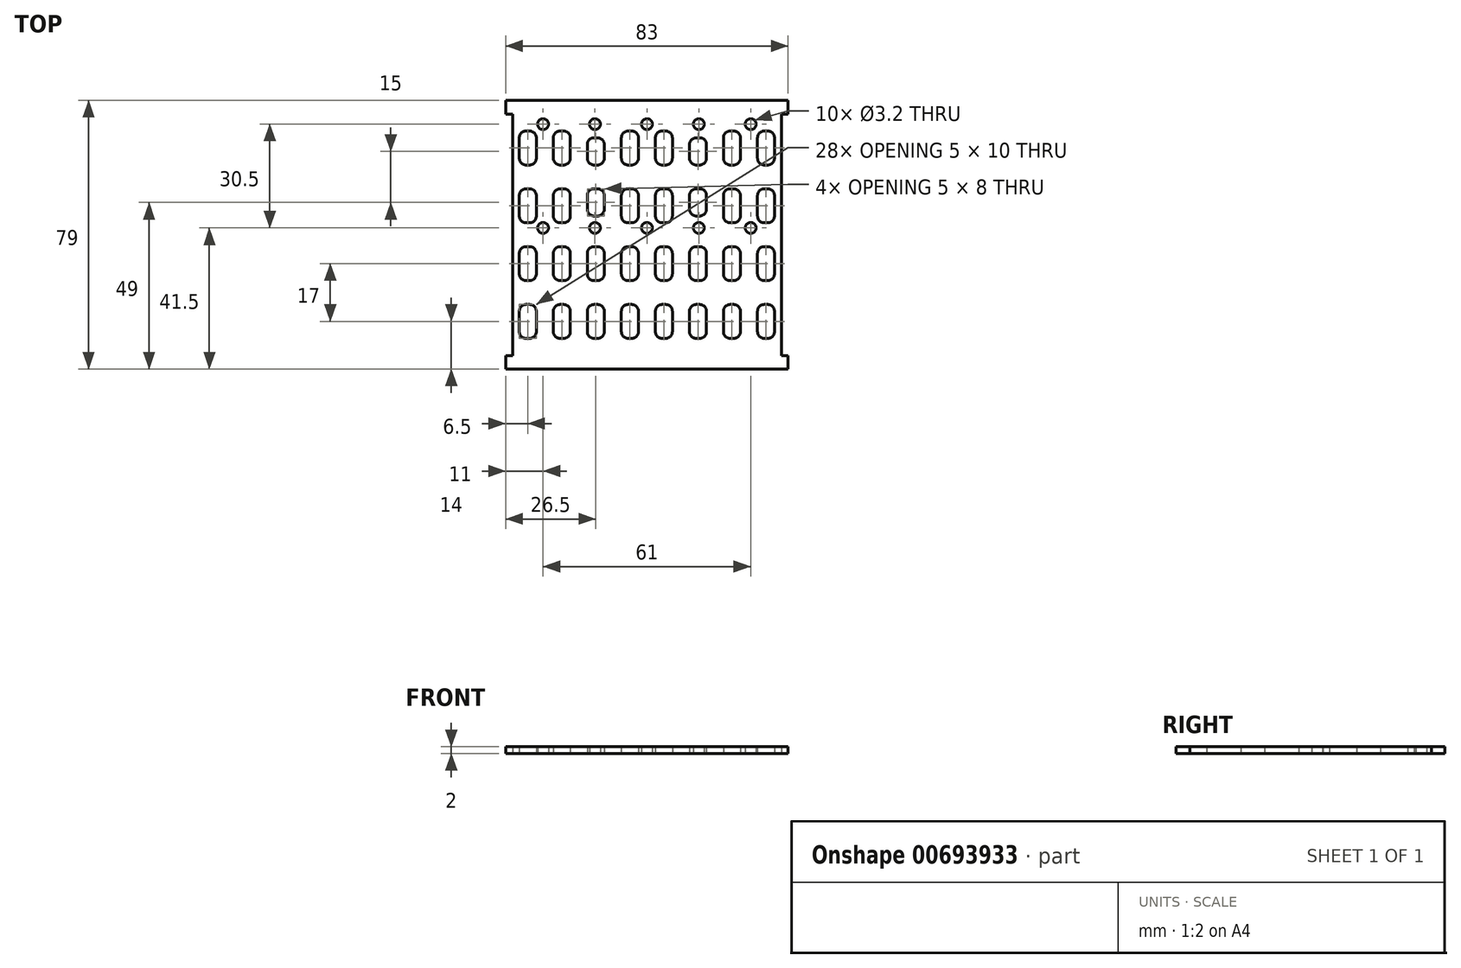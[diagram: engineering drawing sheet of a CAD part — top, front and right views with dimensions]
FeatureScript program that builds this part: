
annotation { "Feature Type Name" : "Feature", "Feature Type Description" : "" }
export const myFeature = defineFeature(function(context is Context, id is Id, definition is map)
    precondition{}
    {
        {
            var Q0;
            Q0=qCreatedBy(makeId("Top.planeOp"),FACE);
            var sketch = newSketch(context, id + "F0", { "sketchPlane" : qUnion([Q0])});
            skLineSegment(sketch, "E0.bottom", {"start": v(39.5, 39.5) * mm, "end": v(-39.5, 39.5) * mm});
            skLineSegment(sketch, "E0.top", {"start": v(39.5, -39.5) * mm, "end": v(-39.5, -39.5) * mm});
            skLineSegment(sketch, "E0.left", {"start": v(39.5, 35.5) * mm, "end": v(39.5, -35.5) * mm});
            skLineSegment(sketch, "E0.right", {"start": v(-39.5, 35.5) * mm, "end": v(-39.5, -35.5) * mm});
            skPoint(sketch, "E0.middle", {"position": v(0, 0) * mm});
            skCircle(sketch, "E1", {"center": v(-30.5, 32.5) * mm, "radius": 1.6 * mm});
            skCircle(sketch, "E2.0.1.0", {"center": v(-30.5, 2) * mm, "radius": 1.6 * mm});
            skCircle(sketch, "E2.1.0.0", {"center": v(-15.25, 32.5) * mm, "radius": 1.6 * mm});
            skCircle(sketch, "E2.1.1.0", {"center": v(-15.25, 2) * mm, "radius": 1.6 * mm});
            skLineSegment(sketch, "E2.direction1", {"start": v(-30.5, 32.5) * mm, "end": v(-15.25, 32.5) * mm, "construction": true});
            skLineSegment(sketch, "E2.direction2", {"start": v(-30.5, 32.5) * mm, "end": v(-30.5, 2) * mm, "construction": true});
            skCircle(sketch, "E3.0.2.0", {"center": v(0, 32.5) * mm, "radius": 1.6 * mm});
            skCircle(sketch, "E3.0.2.1", {"center": v(0, 2) * mm, "radius": 1.6 * mm});
            skCircle(sketch, "E3.0.3.0", {"center": v(15.25, 32.5) * mm, "radius": 1.6 * mm});
            skCircle(sketch, "E3.0.3.1", {"center": v(15.25, 2) * mm, "radius": 1.6 * mm});
            skCircle(sketch, "E3.0.4.0", {"center": v(30.5, 32.5) * mm, "radius": 1.6 * mm});
            skCircle(sketch, "E3.0.4.1", {"center": v(30.5, 2) * mm, "radius": 1.6 * mm});
            skLineSegment(sketch, "E4.bottom", {"start": v(-5.5, -3.5) * mm, "end": v(-4.5, -3.5) * mm});
            skLineSegment(sketch, "E4.top", {"start": v(-5.5, -13.5) * mm, "end": v(-4.5, -13.5) * mm});
            skLineSegment(sketch, "E4.left", {"start": v(-7.5, -5.5) * mm, "end": v(-7.5, -11.5) * mm});
            skLineSegment(sketch, "E4.right", {"start": v(-2.5, -5.5) * mm, "end": v(-2.5, -11.5) * mm});
            skPoint(sketch, "E5.visualSharp", {"position": v(-7.5, -3.5) * mm});
            skArc(sketch, "E5.filletArc", {"start": v(-5.5, -3.5) * mm, "mid": v(-6.91, -4.09) * mm, "end": v(-7.5, -5.5) * mm});
            skPoint(sketch, "E6.visualSharp", {"position": v(-2.5, -3.5) * mm});
            skArc(sketch, "E6.filletArc", {"start": v(-2.5, -5.5) * mm, "mid": v(-3.09, -4.09) * mm, "end": v(-4.5, -3.5) * mm});
            skPoint(sketch, "E7.visualSharp", {"position": v(-7.5, -13.5) * mm});
            skArc(sketch, "E7.filletArc", {"start": v(-7.5, -11.5) * mm, "mid": v(-6.91, -12.91) * mm, "end": v(-5.5, -13.5) * mm});
            skPoint(sketch, "E8.visualSharp", {"position": v(-2.5, -13.5) * mm});
            skArc(sketch, "E8.filletArc", {"start": v(-4.5, -13.5) * mm, "mid": v(-3.09, -12.91) * mm, "end": v(-2.5, -11.5) * mm});
            skLineSegment(sketch, "E9.0.1.0", {"start": v(-7.5, -22.5) * mm, "end": v(-7.5, -28.5) * mm});
            skLineSegment(sketch, "E9.0.1.1", {"start": v(-2.5, -22.5) * mm, "end": v(-2.5, -28.5) * mm});
            skArc(sketch, "E9.0.1.2", {"start": v(-2.5, -22.5) * mm, "mid": v(-3.09, -21.09) * mm, "end": v(-4.5, -20.5) * mm});
            skLineSegment(sketch, "E9.0.1.3", {"start": v(-5.5, -20.5) * mm, "end": v(-4.5, -20.5) * mm});
            skArc(sketch, "E9.0.1.4", {"start": v(-5.5, -20.5) * mm, "mid": v(-6.91, -21.09) * mm, "end": v(-7.5, -22.5) * mm});
            skArc(sketch, "E9.0.1.5", {"start": v(-7.5, -28.5) * mm, "mid": v(-6.91, -29.91) * mm, "end": v(-5.5, -30.5) * mm});
            skLineSegment(sketch, "E9.0.1.6", {"start": v(-5.5, -30.5) * mm, "end": v(-4.5, -30.5) * mm});
            skArc(sketch, "E9.0.1.7", {"start": v(-4.5, -30.5) * mm, "mid": v(-3.09, -29.91) * mm, "end": v(-2.5, -28.5) * mm});
            skLineSegment(sketch, "E9.1.0.0", {"start": v(-17.5, -5.5) * mm, "end": v(-17.5, -11.5) * mm});
            skLineSegment(sketch, "E9.1.0.1", {"start": v(-12.5, -5.5) * mm, "end": v(-12.5, -11.5) * mm});
            skArc(sketch, "E9.1.0.2", {"start": v(-12.5, -5.5) * mm, "mid": v(-13.09, -4.09) * mm, "end": v(-14.5, -3.5) * mm});
            skLineSegment(sketch, "E9.1.0.3", {"start": v(-15.5, -3.5) * mm, "end": v(-14.5, -3.5) * mm});
            skArc(sketch, "E9.1.0.4", {"start": v(-15.5, -3.5) * mm, "mid": v(-16.91, -4.09) * mm, "end": v(-17.5, -5.5) * mm});
            skArc(sketch, "E9.1.0.5", {"start": v(-17.5, -11.5) * mm, "mid": v(-16.91, -12.91) * mm, "end": v(-15.5, -13.5) * mm});
            skLineSegment(sketch, "E9.1.0.6", {"start": v(-15.5, -13.5) * mm, "end": v(-14.5, -13.5) * mm});
            skArc(sketch, "E9.1.0.7", {"start": v(-14.5, -13.5) * mm, "mid": v(-13.09, -12.91) * mm, "end": v(-12.5, -11.5) * mm});
            skLineSegment(sketch, "E9.1.1.0", {"start": v(-17.5, -22.5) * mm, "end": v(-17.5, -28.5) * mm});
            skLineSegment(sketch, "E9.1.1.1", {"start": v(-12.5, -22.5) * mm, "end": v(-12.5, -28.5) * mm});
            skArc(sketch, "E9.1.1.2", {"start": v(-12.5, -22.5) * mm, "mid": v(-13.09, -21.09) * mm, "end": v(-14.5, -20.5) * mm});
            skLineSegment(sketch, "E9.1.1.3", {"start": v(-15.5, -20.5) * mm, "end": v(-14.5, -20.5) * mm});
            skArc(sketch, "E9.1.1.4", {"start": v(-15.5, -20.5) * mm, "mid": v(-16.91, -21.09) * mm, "end": v(-17.5, -22.5) * mm});
            skArc(sketch, "E9.1.1.5", {"start": v(-17.5, -28.5) * mm, "mid": v(-16.91, -29.91) * mm, "end": v(-15.5, -30.5) * mm});
            skLineSegment(sketch, "E9.1.1.6", {"start": v(-15.5, -30.5) * mm, "end": v(-14.5, -30.5) * mm});
            skArc(sketch, "E9.1.1.7", {"start": v(-14.5, -30.5) * mm, "mid": v(-13.09, -29.91) * mm, "end": v(-12.5, -28.5) * mm});
            skLineSegment(sketch, "E9.2.0.0", {"start": v(-27.5, -5.5) * mm, "end": v(-27.5, -11.5) * mm});
            skLineSegment(sketch, "E9.2.0.1", {"start": v(-22.5, -5.5) * mm, "end": v(-22.5, -11.5) * mm});
            skArc(sketch, "E9.2.0.2", {"start": v(-22.5, -5.5) * mm, "mid": v(-23.09, -4.09) * mm, "end": v(-24.5, -3.5) * mm});
            skLineSegment(sketch, "E9.2.0.3", {"start": v(-25.5, -3.5) * mm, "end": v(-24.5, -3.5) * mm});
            skArc(sketch, "E9.2.0.4", {"start": v(-25.5, -3.5) * mm, "mid": v(-26.91, -4.09) * mm, "end": v(-27.5, -5.5) * mm});
            skArc(sketch, "E9.2.0.5", {"start": v(-27.5, -11.5) * mm, "mid": v(-26.91, -12.91) * mm, "end": v(-25.5, -13.5) * mm});
            skLineSegment(sketch, "E9.2.0.6", {"start": v(-25.5, -13.5) * mm, "end": v(-24.5, -13.5) * mm});
            skArc(sketch, "E9.2.0.7", {"start": v(-24.5, -13.5) * mm, "mid": v(-23.09, -12.91) * mm, "end": v(-22.5, -11.5) * mm});
            skLineSegment(sketch, "E9.2.1.0", {"start": v(-27.5, -22.5) * mm, "end": v(-27.5, -28.5) * mm});
            skLineSegment(sketch, "E9.2.1.1", {"start": v(-22.5, -22.5) * mm, "end": v(-22.5, -28.5) * mm});
            skArc(sketch, "E9.2.1.2", {"start": v(-22.5, -22.5) * mm, "mid": v(-23.09, -21.09) * mm, "end": v(-24.5, -20.5) * mm});
            skLineSegment(sketch, "E9.2.1.3", {"start": v(-25.5, -20.5) * mm, "end": v(-24.5, -20.5) * mm});
            skArc(sketch, "E9.2.1.4", {"start": v(-25.5, -20.5) * mm, "mid": v(-26.91, -21.09) * mm, "end": v(-27.5, -22.5) * mm});
            skArc(sketch, "E9.2.1.5", {"start": v(-27.5, -28.5) * mm, "mid": v(-26.91, -29.91) * mm, "end": v(-25.5, -30.5) * mm});
            skLineSegment(sketch, "E9.2.1.6", {"start": v(-25.5, -30.5) * mm, "end": v(-24.5, -30.5) * mm});
            skArc(sketch, "E9.2.1.7", {"start": v(-24.5, -30.5) * mm, "mid": v(-23.09, -29.91) * mm, "end": v(-22.5, -28.5) * mm});
            skLineSegment(sketch, "E9.3.0.0", {"start": v(-37.5, -5.5) * mm, "end": v(-37.5, -11.5) * mm});
            skLineSegment(sketch, "E9.3.0.1", {"start": v(-32.5, -5.5) * mm, "end": v(-32.5, -11.5) * mm});
            skArc(sketch, "E9.3.0.2", {"start": v(-32.5, -5.5) * mm, "mid": v(-33.09, -4.09) * mm, "end": v(-34.5, -3.5) * mm});
            skLineSegment(sketch, "E9.3.0.3", {"start": v(-35.5, -3.5) * mm, "end": v(-34.5, -3.5) * mm});
            skArc(sketch, "E9.3.0.4", {"start": v(-35.5, -3.5) * mm, "mid": v(-36.91, -4.09) * mm, "end": v(-37.5, -5.5) * mm});
            skArc(sketch, "E9.3.0.5", {"start": v(-37.5, -11.5) * mm, "mid": v(-36.91, -12.91) * mm, "end": v(-35.5, -13.5) * mm});
            skLineSegment(sketch, "E9.3.0.6", {"start": v(-35.5, -13.5) * mm, "end": v(-34.5, -13.5) * mm});
            skArc(sketch, "E9.3.0.7", {"start": v(-34.5, -13.5) * mm, "mid": v(-33.09, -12.91) * mm, "end": v(-32.5, -11.5) * mm});
            skLineSegment(sketch, "E9.3.1.0", {"start": v(-37.5, -22.5) * mm, "end": v(-37.5, -28.5) * mm});
            skLineSegment(sketch, "E9.3.1.1", {"start": v(-32.5, -22.5) * mm, "end": v(-32.5, -28.5) * mm});
            skArc(sketch, "E9.3.1.2", {"start": v(-32.5, -22.5) * mm, "mid": v(-33.09, -21.09) * mm, "end": v(-34.5, -20.5) * mm});
            skLineSegment(sketch, "E9.3.1.3", {"start": v(-35.5, -20.5) * mm, "end": v(-34.5, -20.5) * mm});
            skArc(sketch, "E9.3.1.4", {"start": v(-35.5, -20.5) * mm, "mid": v(-36.91, -21.09) * mm, "end": v(-37.5, -22.5) * mm});
            skArc(sketch, "E9.3.1.5", {"start": v(-37.5, -28.5) * mm, "mid": v(-36.91, -29.91) * mm, "end": v(-35.5, -30.5) * mm});
            skLineSegment(sketch, "E9.3.1.6", {"start": v(-35.5, -30.5) * mm, "end": v(-34.5, -30.5) * mm});
            skArc(sketch, "E9.3.1.7", {"start": v(-34.5, -30.5) * mm, "mid": v(-33.09, -29.91) * mm, "end": v(-32.5, -28.5) * mm});
            skLineSegment(sketch, "E9.direction1", {"start": v(-7.5, -11.5) * mm, "end": v(-17.5, -11.5) * mm, "construction": true});
            skLineSegment(sketch, "E9.direction2", {"start": v(-7.5, -11.5) * mm, "end": v(-7.5, -28.5) * mm, "construction": true});
            skLineSegment(sketch, "E10.0.1.0", {"start": v(-37.5, 28.5) * mm, "end": v(-37.5, 22.5) * mm});
            skLineSegment(sketch, "E10.0.1.1", {"start": v(-22.5, 11.5) * mm, "end": v(-22.5, 5.5) * mm});
            skLineSegment(sketch, "E10.0.1.2", {"start": v(-12.5, 11.5) * mm, "end": v(-12.5, 7.5) * mm});
            skLineSegment(sketch, "E10.0.1.3", {"start": v(-2.5, 28.5) * mm, "end": v(-2.5, 22.5) * mm});
            skLineSegment(sketch, "E10.0.1.4", {"start": v(-2.5, 11.5) * mm, "end": v(-2.5, 5.5) * mm});
            skLineSegment(sketch, "E10.0.1.5", {"start": v(-12.5, 26.5) * mm, "end": v(-12.5, 22.5) * mm});
            skLineSegment(sketch, "E10.0.1.6", {"start": v(-27.5, 11.5) * mm, "end": v(-27.5, 5.5) * mm});
            skLineSegment(sketch, "E10.0.1.7", {"start": v(-27.5, 28.5) * mm, "end": v(-27.5, 22.5) * mm});
            skLineSegment(sketch, "E10.0.1.8", {"start": v(-32.5, 11.5) * mm, "end": v(-32.5, 5.5) * mm});
            skLineSegment(sketch, "E10.0.1.9", {"start": v(-7.5, 28.5) * mm, "end": v(-7.5, 22.5) * mm});
            skLineSegment(sketch, "E10.0.1.10", {"start": v(-17.5, 11.5) * mm, "end": v(-17.5, 7.5) * mm});
            skLineSegment(sketch, "E10.0.1.11", {"start": v(-22.5, 28.5) * mm, "end": v(-22.5, 22.5) * mm});
            skLineSegment(sketch, "E10.0.1.12", {"start": v(-7.5, 22.5) * mm, "end": v(-17.5, 22.5) * mm, "construction": true});
            skLineSegment(sketch, "E10.0.1.13", {"start": v(-37.5, 11.5) * mm, "end": v(-37.5, 5.5) * mm});
            skLineSegment(sketch, "E10.0.1.14", {"start": v(-32.5, 28.5) * mm, "end": v(-32.5, 22.5) * mm});
            skLineSegment(sketch, "E10.0.1.15", {"start": v(-17.5, 26.5) * mm, "end": v(-17.5, 22.5) * mm});
            skLineSegment(sketch, "E10.0.1.16", {"start": v(-7.5, 11.5) * mm, "end": v(-7.5, 5.5) * mm});
            skArc(sketch, "E10.0.1.17", {"start": v(-32.5, 11.5) * mm, "mid": v(-33.09, 12.91) * mm, "end": v(-34.5, 13.5) * mm});
            skArc(sketch, "E10.0.1.18", {"start": v(-2.5, 28.5) * mm, "mid": v(-3.09, 29.91) * mm, "end": v(-4.5, 30.5) * mm});
            skLineSegment(sketch, "E10.0.1.19", {"start": v(-25.5, 13.5) * mm, "end": v(-24.5, 13.5) * mm});
            skArc(sketch, "E10.0.1.20", {"start": v(-2.5, 11.5) * mm, "mid": v(-3.09, 12.91) * mm, "end": v(-4.5, 13.5) * mm});
            skArc(sketch, "E10.0.1.21", {"start": v(-37.5, 5.5) * mm, "mid": v(-36.91, 4.09) * mm, "end": v(-35.5, 3.5) * mm});
            skArc(sketch, "E10.0.1.22", {"start": v(-32.5, 28.5) * mm, "mid": v(-33.09, 29.91) * mm, "end": v(-34.5, 30.5) * mm});
            skArc(sketch, "E10.0.1.23", {"start": v(-35.5, 13.5) * mm, "mid": v(-36.91, 12.91) * mm, "end": v(-37.5, 11.5) * mm});
            skLineSegment(sketch, "E10.0.1.24", {"start": v(-5.5, 13.5) * mm, "end": v(-4.5, 13.5) * mm});
            skArc(sketch, "E10.0.1.25", {"start": v(-22.5, 28.5) * mm, "mid": v(-23.09, 29.91) * mm, "end": v(-24.5, 30.5) * mm});
            skArc(sketch, "E10.0.1.26", {"start": v(-15.5, 13.5) * mm, "mid": v(-16.91, 12.91) * mm, "end": v(-17.5, 11.5) * mm});
            skLineSegment(sketch, "E10.0.1.27", {"start": v(-35.5, 30.5) * mm, "end": v(-34.5, 30.5) * mm});
            skArc(sketch, "E10.0.1.28", {"start": v(-12.5, 11.5) * mm, "mid": v(-13.09, 12.91) * mm, "end": v(-14.5, 13.5) * mm});
            skLineSegment(sketch, "E10.0.1.29", {"start": v(-35.5, 13.5) * mm, "end": v(-34.5, 13.5) * mm});
            skArc(sketch, "E10.0.1.32", {"start": v(-4.5, 3.5) * mm, "mid": v(-3.09, 4.09) * mm, "end": v(-2.5, 5.5) * mm});
            skArc(sketch, "E10.0.1.33", {"start": v(-5.5, 13.5) * mm, "mid": v(-6.91, 12.91) * mm, "end": v(-7.5, 11.5) * mm});
            skArc(sketch, "E10.0.1.34", {"start": v(-5.5, 30.5) * mm, "mid": v(-6.91, 29.91) * mm, "end": v(-7.5, 28.5) * mm});
            skArc(sketch, "E10.0.1.35", {"start": v(-35.5, 30.5) * mm, "mid": v(-36.91, 29.91) * mm, "end": v(-37.5, 28.5) * mm});
            skLineSegment(sketch, "E10.0.1.36", {"start": v(-35.5, 20.5) * mm, "end": v(-34.5, 20.5) * mm});
            skArc(sketch, "E10.0.1.38", {"start": v(-34.5, 3.5) * mm, "mid": v(-33.09, 4.09) * mm, "end": v(-32.5, 5.5) * mm});
            skArc(sketch, "E10.0.1.39", {"start": v(-37.5, 22.5) * mm, "mid": v(-36.91, 21.09) * mm, "end": v(-35.5, 20.5) * mm});
            skArc(sketch, "E10.0.1.40", {"start": v(-14.5, 20.5) * mm, "mid": v(-13.09, 21.09) * mm, "end": v(-12.5, 22.5) * mm});
            skLineSegment(sketch, "E10.0.1.42", {"start": v(-15.5, 13.5) * mm, "end": v(-14.5, 13.5) * mm});
            skArc(sketch, "E10.0.1.43", {"start": v(-22.5, 11.5) * mm, "mid": v(-23.09, 12.91) * mm, "end": v(-24.5, 13.5) * mm});
            skArc(sketch, "E10.0.1.44", {"start": v(-25.5, 30.5) * mm, "mid": v(-26.91, 29.91) * mm, "end": v(-27.5, 28.5) * mm});
            skArc(sketch, "E10.0.1.45", {"start": v(-27.5, 5.5) * mm, "mid": v(-26.91, 4.09) * mm, "end": v(-25.5, 3.5) * mm});
            skArc(sketch, "E10.0.1.46", {"start": v(-4.5, 20.5) * mm, "mid": v(-3.09, 21.09) * mm, "end": v(-2.5, 22.5) * mm});
            skLineSegment(sketch, "E10.0.1.47", {"start": v(-25.5, 20.5) * mm, "end": v(-24.5, 20.5) * mm});
            skLineSegment(sketch, "E10.0.1.48", {"start": v(-5.5, 3.5) * mm, "end": v(-4.5, 3.5) * mm});
            skArc(sketch, "E10.0.1.50", {"start": v(-24.5, 20.5) * mm, "mid": v(-23.09, 21.09) * mm, "end": v(-22.5, 22.5) * mm});
            skArc(sketch, "E10.0.1.51", {"start": v(-34.5, 20.5) * mm, "mid": v(-33.09, 21.09) * mm, "end": v(-32.5, 22.5) * mm});
            skArc(sketch, "E10.0.1.53", {"start": v(-17.5, 22.5) * mm, "mid": v(-16.91, 21.09) * mm, "end": v(-15.5, 20.5) * mm});
            skArc(sketch, "E10.0.1.54", {"start": v(-24.5, 3.5) * mm, "mid": v(-23.09, 4.09) * mm, "end": v(-22.5, 5.5) * mm});
            skLineSegment(sketch, "E10.0.1.55", {"start": v(-35.5, 3.5) * mm, "end": v(-34.5, 3.5) * mm});
            skLineSegment(sketch, "E10.0.1.56", {"start": v(-15.5, 20.5) * mm, "end": v(-14.5, 20.5) * mm});
            skLineSegment(sketch, "E10.0.1.57", {"start": v(-25.5, 30.5) * mm, "end": v(-24.5, 30.5) * mm});
            skArc(sketch, "E10.0.1.58", {"start": v(-7.5, 5.5) * mm, "mid": v(-6.91, 4.09) * mm, "end": v(-5.5, 3.5) * mm});
            skArc(sketch, "E10.0.1.59", {"start": v(-27.5, 22.5) * mm, "mid": v(-26.91, 21.09) * mm, "end": v(-25.5, 20.5) * mm});
            skArc(sketch, "E10.0.1.60", {"start": v(-25.5, 13.5) * mm, "mid": v(-26.91, 12.91) * mm, "end": v(-27.5, 11.5) * mm});
            skLineSegment(sketch, "E10.0.1.61", {"start": v(-25.5, 3.5) * mm, "end": v(-24.5, 3.5) * mm});
            skArc(sketch, "E10.0.1.62", {"start": v(-7.5, 22.5) * mm, "mid": v(-6.91, 21.09) * mm, "end": v(-5.5, 20.5) * mm});
            skLineSegment(sketch, "E10.0.1.63", {"start": v(-5.5, 20.5) * mm, "end": v(-4.5, 20.5) * mm});
            skLineSegment(sketch, "E10.0.1.64", {"start": v(-5.5, 30.5) * mm, "end": v(-4.5, 30.5) * mm});
            skLineSegment(sketch, "E10.1.0.0", {"start": v(2.5, -5.5) * mm, "end": v(2.5, -11.5) * mm});
            skLineSegment(sketch, "E10.1.0.1", {"start": v(17.5, -22.5) * mm, "end": v(17.5, -28.5) * mm});
            skLineSegment(sketch, "E10.1.0.2", {"start": v(27.5, -22.5) * mm, "end": v(27.5, -28.5) * mm});
            skLineSegment(sketch, "E10.1.0.3", {"start": v(37.5, -5.5) * mm, "end": v(37.5, -11.5) * mm});
            skLineSegment(sketch, "E10.1.0.4", {"start": v(37.5, -22.5) * mm, "end": v(37.5, -28.5) * mm});
            skLineSegment(sketch, "E10.1.0.5", {"start": v(27.5, -5.5) * mm, "end": v(27.5, -11.5) * mm});
            skLineSegment(sketch, "E10.1.0.6", {"start": v(12.5, -22.5) * mm, "end": v(12.5, -28.5) * mm});
            skLineSegment(sketch, "E10.1.0.7", {"start": v(12.5, -5.5) * mm, "end": v(12.5, -11.5) * mm});
            skLineSegment(sketch, "E10.1.0.8", {"start": v(7.5, -22.5) * mm, "end": v(7.5, -28.5) * mm});
            skLineSegment(sketch, "E10.1.0.9", {"start": v(32.5, -5.5) * mm, "end": v(32.5, -11.5) * mm});
            skLineSegment(sketch, "E10.1.0.10", {"start": v(22.5, -22.5) * mm, "end": v(22.5, -28.5) * mm});
            skLineSegment(sketch, "E10.1.0.11", {"start": v(17.5, -5.5) * mm, "end": v(17.5, -11.5) * mm});
            skLineSegment(sketch, "E10.1.0.12", {"start": v(32.5, -11.5) * mm, "end": v(22.5, -11.5) * mm, "construction": true});
            skLineSegment(sketch, "E10.1.0.13", {"start": v(2.5, -22.5) * mm, "end": v(2.5, -28.5) * mm});
            skLineSegment(sketch, "E10.1.0.14", {"start": v(7.5, -5.5) * mm, "end": v(7.5, -11.5) * mm});
            skLineSegment(sketch, "E10.1.0.15", {"start": v(22.5, -5.5) * mm, "end": v(22.5, -11.5) * mm});
            skLineSegment(sketch, "E10.1.0.16", {"start": v(32.5, -22.5) * mm, "end": v(32.5, -28.5) * mm});
            skArc(sketch, "E10.1.0.17", {"start": v(7.5, -22.5) * mm, "mid": v(6.91, -21.09) * mm, "end": v(5.5, -20.5) * mm});
            skArc(sketch, "E10.1.0.18", {"start": v(37.5, -5.5) * mm, "mid": v(36.91, -4.09) * mm, "end": v(35.5, -3.5) * mm});
            skLineSegment(sketch, "E10.1.0.19", {"start": v(14.5, -20.5) * mm, "end": v(15.5, -20.5) * mm});
            skArc(sketch, "E10.1.0.20", {"start": v(37.5, -22.5) * mm, "mid": v(36.91, -21.09) * mm, "end": v(35.5, -20.5) * mm});
            skArc(sketch, "E10.1.0.21", {"start": v(2.5, -28.5) * mm, "mid": v(3.09, -29.91) * mm, "end": v(4.5, -30.5) * mm});
            skArc(sketch, "E10.1.0.22", {"start": v(7.5, -5.5) * mm, "mid": v(6.91, -4.09) * mm, "end": v(5.5, -3.5) * mm});
            skArc(sketch, "E10.1.0.23", {"start": v(4.5, -20.5) * mm, "mid": v(3.09, -21.09) * mm, "end": v(2.5, -22.5) * mm});
            skLineSegment(sketch, "E10.1.0.24", {"start": v(34.5, -20.5) * mm, "end": v(35.5, -20.5) * mm});
            skArc(sketch, "E10.1.0.25", {"start": v(17.5, -5.5) * mm, "mid": v(16.91, -4.09) * mm, "end": v(15.5, -3.5) * mm});
            skArc(sketch, "E10.1.0.26", {"start": v(24.5, -20.5) * mm, "mid": v(23.09, -21.09) * mm, "end": v(22.5, -22.5) * mm});
            skLineSegment(sketch, "E10.1.0.27", {"start": v(4.5, -3.5) * mm, "end": v(5.5, -3.5) * mm});
            skArc(sketch, "E10.1.0.28", {"start": v(27.5, -22.5) * mm, "mid": v(26.91, -21.09) * mm, "end": v(25.5, -20.5) * mm});
            skLineSegment(sketch, "E10.1.0.29", {"start": v(4.5, -20.5) * mm, "end": v(5.5, -20.5) * mm});
            skArc(sketch, "E10.1.0.30", {"start": v(27.5, -5.5) * mm, "mid": v(26.91, -4.09) * mm, "end": v(25.5, -3.5) * mm});
            skLineSegment(sketch, "E10.1.0.31", {"start": v(24.5, -30.5) * mm, "end": v(25.5, -30.5) * mm});
            skArc(sketch, "E10.1.0.32", {"start": v(35.5, -30.5) * mm, "mid": v(36.91, -29.91) * mm, "end": v(37.5, -28.5) * mm});
            skArc(sketch, "E10.1.0.33", {"start": v(34.5, -20.5) * mm, "mid": v(33.09, -21.09) * mm, "end": v(32.5, -22.5) * mm});
            skArc(sketch, "E10.1.0.34", {"start": v(34.5, -3.5) * mm, "mid": v(33.09, -4.09) * mm, "end": v(32.5, -5.5) * mm});
            skArc(sketch, "E10.1.0.35", {"start": v(4.5, -3.5) * mm, "mid": v(3.09, -4.09) * mm, "end": v(2.5, -5.5) * mm});
            skLineSegment(sketch, "E10.1.0.36", {"start": v(4.5, -13.5) * mm, "end": v(5.5, -13.5) * mm});
            skArc(sketch, "E10.1.0.37", {"start": v(24.5, -3.5) * mm, "mid": v(23.09, -4.09) * mm, "end": v(22.5, -5.5) * mm});
            skArc(sketch, "E10.1.0.38", {"start": v(5.5, -30.5) * mm, "mid": v(6.91, -29.91) * mm, "end": v(7.5, -28.5) * mm});
            skArc(sketch, "E10.1.0.39", {"start": v(2.5, -11.5) * mm, "mid": v(3.09, -12.91) * mm, "end": v(4.5, -13.5) * mm});
            skArc(sketch, "E10.1.0.40", {"start": v(25.5, -13.5) * mm, "mid": v(26.91, -12.91) * mm, "end": v(27.5, -11.5) * mm});
            skLineSegment(sketch, "E10.1.0.41", {"start": v(24.5, -3.5) * mm, "end": v(25.5, -3.5) * mm});
            skLineSegment(sketch, "E10.1.0.42", {"start": v(24.5, -20.5) * mm, "end": v(25.5, -20.5) * mm});
            skArc(sketch, "E10.1.0.43", {"start": v(17.5, -22.5) * mm, "mid": v(16.91, -21.09) * mm, "end": v(15.5, -20.5) * mm});
            skArc(sketch, "E10.1.0.44", {"start": v(14.5, -3.5) * mm, "mid": v(13.09, -4.09) * mm, "end": v(12.5, -5.5) * mm});
            skArc(sketch, "E10.1.0.45", {"start": v(12.5, -28.5) * mm, "mid": v(13.09, -29.91) * mm, "end": v(14.5, -30.5) * mm});
            skArc(sketch, "E10.1.0.46", {"start": v(35.5, -13.5) * mm, "mid": v(36.91, -12.91) * mm, "end": v(37.5, -11.5) * mm});
            skLineSegment(sketch, "E10.1.0.47", {"start": v(14.5, -13.5) * mm, "end": v(15.5, -13.5) * mm});
            skLineSegment(sketch, "E10.1.0.48", {"start": v(34.5, -30.5) * mm, "end": v(35.5, -30.5) * mm});
            skArc(sketch, "E10.1.0.49", {"start": v(25.5, -30.5) * mm, "mid": v(26.91, -29.91) * mm, "end": v(27.5, -28.5) * mm});
            skArc(sketch, "E10.1.0.50", {"start": v(15.5, -13.5) * mm, "mid": v(16.91, -12.91) * mm, "end": v(17.5, -11.5) * mm});
            skArc(sketch, "E10.1.0.51", {"start": v(5.5, -13.5) * mm, "mid": v(6.91, -12.91) * mm, "end": v(7.5, -11.5) * mm});
            skArc(sketch, "E10.1.0.52", {"start": v(22.5, -28.5) * mm, "mid": v(23.09, -29.91) * mm, "end": v(24.5, -30.5) * mm});
            skArc(sketch, "E10.1.0.53", {"start": v(22.5, -11.5) * mm, "mid": v(23.09, -12.91) * mm, "end": v(24.5, -13.5) * mm});
            skArc(sketch, "E10.1.0.54", {"start": v(15.5, -30.5) * mm, "mid": v(16.91, -29.91) * mm, "end": v(17.5, -28.5) * mm});
            skLineSegment(sketch, "E10.1.0.55", {"start": v(4.5, -30.5) * mm, "end": v(5.5, -30.5) * mm});
            skLineSegment(sketch, "E10.1.0.56", {"start": v(24.5, -13.5) * mm, "end": v(25.5, -13.5) * mm});
            skLineSegment(sketch, "E10.1.0.57", {"start": v(14.5, -3.5) * mm, "end": v(15.5, -3.5) * mm});
            skArc(sketch, "E10.1.0.58", {"start": v(32.5, -28.5) * mm, "mid": v(33.09, -29.91) * mm, "end": v(34.5, -30.5) * mm});
            skArc(sketch, "E10.1.0.59", {"start": v(12.5, -11.5) * mm, "mid": v(13.09, -12.91) * mm, "end": v(14.5, -13.5) * mm});
            skArc(sketch, "E10.1.0.60", {"start": v(14.5, -20.5) * mm, "mid": v(13.09, -21.09) * mm, "end": v(12.5, -22.5) * mm});
            skLineSegment(sketch, "E10.1.0.61", {"start": v(14.5, -30.5) * mm, "end": v(15.5, -30.5) * mm});
            skArc(sketch, "E10.1.0.62", {"start": v(32.5, -11.5) * mm, "mid": v(33.09, -12.91) * mm, "end": v(34.5, -13.5) * mm});
            skLineSegment(sketch, "E10.1.0.63", {"start": v(34.5, -13.5) * mm, "end": v(35.5, -13.5) * mm});
            skLineSegment(sketch, "E10.1.0.64", {"start": v(34.5, -3.5) * mm, "end": v(35.5, -3.5) * mm});
            skLineSegment(sketch, "E10.1.1.0", {"start": v(2.5, 28.5) * mm, "end": v(2.5, 22.5) * mm});
            skLineSegment(sketch, "E10.1.1.1", {"start": v(17.5, 11.5) * mm, "end": v(17.5, 7.5) * mm});
            skLineSegment(sketch, "E10.1.1.2", {"start": v(27.5, 11.5) * mm, "end": v(27.5, 5.5) * mm});
            skLineSegment(sketch, "E10.1.1.3", {"start": v(37.5, 28.5) * mm, "end": v(37.5, 22.5) * mm});
            skLineSegment(sketch, "E10.1.1.4", {"start": v(37.5, 11.5) * mm, "end": v(37.5, 5.5) * mm});
            skLineSegment(sketch, "E10.1.1.5", {"start": v(27.5, 28.5) * mm, "end": v(27.5, 22.5) * mm});
            skLineSegment(sketch, "E10.1.1.6", {"start": v(12.5, 11.5) * mm, "end": v(12.5, 7.5) * mm});
            skLineSegment(sketch, "E10.1.1.7", {"start": v(12.5, 26.5) * mm, "end": v(12.5, 22.5) * mm});
            skLineSegment(sketch, "E10.1.1.8", {"start": v(7.5, 11.5) * mm, "end": v(7.5, 5.5) * mm});
            skLineSegment(sketch, "E10.1.1.9", {"start": v(32.5, 28.5) * mm, "end": v(32.5, 22.5) * mm});
            skLineSegment(sketch, "E10.1.1.10", {"start": v(22.5, 11.5) * mm, "end": v(22.5, 5.5) * mm});
            skLineSegment(sketch, "E10.1.1.11", {"start": v(17.5, 26.5) * mm, "end": v(17.5, 22.5) * mm});
            skLineSegment(sketch, "E10.1.1.12", {"start": v(32.5, 22.5) * mm, "end": v(22.5, 22.5) * mm, "construction": true});
            skLineSegment(sketch, "E10.1.1.13", {"start": v(2.5, 11.5) * mm, "end": v(2.5, 5.5) * mm});
            skLineSegment(sketch, "E10.1.1.14", {"start": v(7.5, 28.5) * mm, "end": v(7.5, 22.5) * mm});
            skLineSegment(sketch, "E10.1.1.15", {"start": v(22.5, 28.5) * mm, "end": v(22.5, 22.5) * mm});
            skLineSegment(sketch, "E10.1.1.16", {"start": v(32.5, 11.5) * mm, "end": v(32.5, 5.5) * mm});
            skArc(sketch, "E10.1.1.17", {"start": v(7.5, 11.5) * mm, "mid": v(6.91, 12.91) * mm, "end": v(5.5, 13.5) * mm});
            skArc(sketch, "E10.1.1.18", {"start": v(37.5, 28.5) * mm, "mid": v(36.91, 29.91) * mm, "end": v(35.5, 30.5) * mm});
            skLineSegment(sketch, "E10.1.1.19", {"start": v(14.5, 13.5) * mm, "end": v(15.5, 13.5) * mm});
            skArc(sketch, "E10.1.1.20", {"start": v(37.5, 11.5) * mm, "mid": v(36.91, 12.91) * mm, "end": v(35.5, 13.5) * mm});
            skArc(sketch, "E10.1.1.21", {"start": v(2.5, 5.5) * mm, "mid": v(3.09, 4.09) * mm, "end": v(4.5, 3.5) * mm});
            skArc(sketch, "E10.1.1.22", {"start": v(7.5, 28.5) * mm, "mid": v(6.91, 29.91) * mm, "end": v(5.5, 30.5) * mm});
            skArc(sketch, "E10.1.1.23", {"start": v(4.5, 13.5) * mm, "mid": v(3.09, 12.91) * mm, "end": v(2.5, 11.5) * mm});
            skLineSegment(sketch, "E10.1.1.24", {"start": v(34.5, 13.5) * mm, "end": v(35.5, 13.5) * mm});
            skArc(sketch, "E10.1.1.26", {"start": v(24.5, 13.5) * mm, "mid": v(23.09, 12.91) * mm, "end": v(22.5, 11.5) * mm});
            skLineSegment(sketch, "E10.1.1.27", {"start": v(4.5, 30.5) * mm, "end": v(5.5, 30.5) * mm});
            skArc(sketch, "E10.1.1.28", {"start": v(27.5, 11.5) * mm, "mid": v(26.91, 12.91) * mm, "end": v(25.5, 13.5) * mm});
            skLineSegment(sketch, "E10.1.1.29", {"start": v(4.5, 13.5) * mm, "end": v(5.5, 13.5) * mm});
            skArc(sketch, "E10.1.1.30", {"start": v(27.5, 28.5) * mm, "mid": v(26.91, 29.91) * mm, "end": v(25.5, 30.5) * mm});
            skLineSegment(sketch, "E10.1.1.31", {"start": v(24.5, 3.5) * mm, "end": v(25.5, 3.5) * mm});
            skArc(sketch, "E10.1.1.32", {"start": v(35.5, 3.5) * mm, "mid": v(36.91, 4.09) * mm, "end": v(37.5, 5.5) * mm});
            skArc(sketch, "E10.1.1.33", {"start": v(34.5, 13.5) * mm, "mid": v(33.09, 12.91) * mm, "end": v(32.5, 11.5) * mm});
            skArc(sketch, "E10.1.1.34", {"start": v(34.5, 30.5) * mm, "mid": v(33.09, 29.91) * mm, "end": v(32.5, 28.5) * mm});
            skArc(sketch, "E10.1.1.35", {"start": v(4.5, 30.5) * mm, "mid": v(3.09, 29.91) * mm, "end": v(2.5, 28.5) * mm});
            skLineSegment(sketch, "E10.1.1.36", {"start": v(4.5, 20.5) * mm, "end": v(5.5, 20.5) * mm});
            skArc(sketch, "E10.1.1.37", {"start": v(24.5, 30.5) * mm, "mid": v(23.09, 29.91) * mm, "end": v(22.5, 28.5) * mm});
            skArc(sketch, "E10.1.1.38", {"start": v(5.5, 3.5) * mm, "mid": v(6.91, 4.09) * mm, "end": v(7.5, 5.5) * mm});
            skArc(sketch, "E10.1.1.39", {"start": v(2.5, 22.5) * mm, "mid": v(3.09, 21.09) * mm, "end": v(4.5, 20.5) * mm});
            skArc(sketch, "E10.1.1.40", {"start": v(25.5, 20.5) * mm, "mid": v(26.91, 21.09) * mm, "end": v(27.5, 22.5) * mm});
            skLineSegment(sketch, "E10.1.1.41", {"start": v(24.5, 30.5) * mm, "end": v(25.5, 30.5) * mm});
            skLineSegment(sketch, "E10.1.1.42", {"start": v(24.5, 13.5) * mm, "end": v(25.5, 13.5) * mm});
            skArc(sketch, "E10.1.1.43", {"start": v(17.5, 11.5) * mm, "mid": v(16.91, 12.91) * mm, "end": v(15.5, 13.5) * mm});
            skArc(sketch, "E10.1.1.46", {"start": v(35.5, 20.5) * mm, "mid": v(36.91, 21.09) * mm, "end": v(37.5, 22.5) * mm});
            skLineSegment(sketch, "E10.1.1.47", {"start": v(14.5, 20.5) * mm, "end": v(15.5, 20.5) * mm});
            skLineSegment(sketch, "E10.1.1.48", {"start": v(34.5, 3.5) * mm, "end": v(35.5, 3.5) * mm});
            skArc(sketch, "E10.1.1.49", {"start": v(25.5, 3.5) * mm, "mid": v(26.91, 4.09) * mm, "end": v(27.5, 5.5) * mm});
            skArc(sketch, "E10.1.1.50", {"start": v(15.5, 20.5) * mm, "mid": v(16.91, 21.09) * mm, "end": v(17.5, 22.5) * mm});
            skArc(sketch, "E10.1.1.51", {"start": v(5.5, 20.5) * mm, "mid": v(6.91, 21.09) * mm, "end": v(7.5, 22.5) * mm});
            skArc(sketch, "E10.1.1.52", {"start": v(22.5, 5.5) * mm, "mid": v(23.09, 4.09) * mm, "end": v(24.5, 3.5) * mm});
            skArc(sketch, "E10.1.1.53", {"start": v(22.5, 22.5) * mm, "mid": v(23.09, 21.09) * mm, "end": v(24.5, 20.5) * mm});
            skLineSegment(sketch, "E10.1.1.55", {"start": v(4.5, 3.5) * mm, "end": v(5.5, 3.5) * mm});
            skLineSegment(sketch, "E10.1.1.56", {"start": v(24.5, 20.5) * mm, "end": v(25.5, 20.5) * mm});
            skArc(sketch, "E10.1.1.58", {"start": v(32.5, 5.5) * mm, "mid": v(33.09, 4.09) * mm, "end": v(34.5, 3.5) * mm});
            skArc(sketch, "E10.1.1.59", {"start": v(12.5, 22.5) * mm, "mid": v(13.09, 21.09) * mm, "end": v(14.5, 20.5) * mm});
            skArc(sketch, "E10.1.1.60", {"start": v(14.5, 13.5) * mm, "mid": v(13.09, 12.91) * mm, "end": v(12.5, 11.5) * mm});
            skArc(sketch, "E10.1.1.62", {"start": v(32.5, 22.5) * mm, "mid": v(33.09, 21.09) * mm, "end": v(34.5, 20.5) * mm});
            skLineSegment(sketch, "E10.1.1.63", {"start": v(34.5, 20.5) * mm, "end": v(35.5, 20.5) * mm});
            skLineSegment(sketch, "E10.1.1.64", {"start": v(34.5, 30.5) * mm, "end": v(35.5, 30.5) * mm});
            skLineSegment(sketch, "E10.direction1", {"start": v(-35.5, -30.5) * mm, "end": v(4.5, -30.5) * mm, "construction": true});
            skLineSegment(sketch, "E10.direction2", {"start": v(-35.5, -30.5) * mm, "end": v(-35.5, 3.5) * mm, "construction": true});
            skLineSegment(sketch, "E11", {"start": v(-15.5, 28.5) * mm, "end": v(-14.5, 28.5) * mm});
            skLineSegment(sketch, "E12", {"start": v(-15.5, 5.5) * mm, "end": v(-14.5, 5.5) * mm});
            skLineSegment(sketch, "E13", {"start": v(14.5, 5.5) * mm, "end": v(15.5, 5.5) * mm});
            skLineSegment(sketch, "E14", {"start": v(14.5, 28.5) * mm, "end": v(15.5, 28.5) * mm});
            skPoint(sketch, "E15.visualSharp", {"position": v(-17.5, 28.5) * mm});
            skArc(sketch, "E15.filletArc", {"start": v(-15.5, 28.5) * mm, "mid": v(-16.91, 27.91) * mm, "end": v(-17.5, 26.5) * mm});
            skPoint(sketch, "E16.visualSharp", {"position": v(-12.5, 28.5) * mm});
            skArc(sketch, "E16.filletArc", {"start": v(-12.5, 26.5) * mm, "mid": v(-13.09, 27.91) * mm, "end": v(-14.5, 28.5) * mm});
            skPoint(sketch, "E17.visualSharp", {"position": v(12.5, 28.5) * mm});
            skArc(sketch, "E17.filletArc", {"start": v(14.5, 28.5) * mm, "mid": v(13.09, 27.91) * mm, "end": v(12.5, 26.5) * mm});
            skPoint(sketch, "E18.visualSharp", {"position": v(12.5, 5.5) * mm});
            skArc(sketch, "E18.filletArc", {"start": v(12.5, 7.5) * mm, "mid": v(13.09, 6.09) * mm, "end": v(14.5, 5.5) * mm});
            skPoint(sketch, "E19.visualSharp", {"position": v(-12.5, 5.5) * mm});
            skArc(sketch, "E19.filletArc", {"start": v(-14.5, 5.5) * mm, "mid": v(-13.09, 6.09) * mm, "end": v(-12.5, 7.5) * mm});
            skPoint(sketch, "E20.visualSharp", {"position": v(-17.5, 5.5) * mm});
            skArc(sketch, "E20.filletArc", {"start": v(-17.5, 7.5) * mm, "mid": v(-16.91, 6.09) * mm, "end": v(-15.5, 5.5) * mm});
            skPoint(sketch, "E21.visualSharp", {"position": v(17.5, 5.5) * mm});
            skArc(sketch, "E21.filletArc", {"start": v(15.5, 5.5) * mm, "mid": v(16.91, 6.09) * mm, "end": v(17.5, 7.5) * mm});
            skPoint(sketch, "E22.visualSharp", {"position": v(17.5, 28.5) * mm});
            skArc(sketch, "E22.filletArc", {"start": v(17.5, 26.5) * mm, "mid": v(16.91, 27.91) * mm, "end": v(15.5, 28.5) * mm});
            skLineSegment(sketch, "E23", {"start": v(39.5, 39.5) * mm, "end": v(41.5, 39.5) * mm});
            skLineSegment(sketch, "E24", {"start": v(41.5, 39.5) * mm, "end": v(41.5, 35.5) * mm});
            skLineSegment(sketch, "E25", {"start": v(41.5, 35.5) * mm, "end": v(39.5, 35.5) * mm});
            skLineSegment(sketch, "E26.MirrorCS", {"start": v(-41.5, 39.5) * mm, "end": v(-41.5, 35.5) * mm});
            skLineSegment(sketch, "E27.MirrorCS", {"start": v(-39.5, 39.5) * mm, "end": v(-41.5, 39.5) * mm});
            skLineSegment(sketch, "E28.MirrorCS", {"start": v(-41.5, 35.5) * mm, "end": v(-39.5, 35.5) * mm});
            skLineSegment(sketch, "E29.MirrorCS", {"start": v(41.5, -35.5) * mm, "end": v(39.5, -35.5) * mm});
            skLineSegment(sketch, "E30.MirrorCS", {"start": v(41.5, -39.5) * mm, "end": v(41.5, -35.5) * mm});
            skLineSegment(sketch, "E31.MirrorCS", {"start": v(39.5, -39.5) * mm, "end": v(41.5, -39.5) * mm});
            skLineSegment(sketch, "E32.MirrorCS", {"start": v(-41.5, -35.5) * mm, "end": v(-39.5, -35.5) * mm});
            skLineSegment(sketch, "E33.MirrorCS", {"start": v(-41.5, -39.5) * mm, "end": v(-41.5, -35.5) * mm});
            skLineSegment(sketch, "E34.MirrorCS", {"start": v(-39.5, -39.5) * mm, "end": v(-41.5, -39.5) * mm});
            skSolve(sketch);
        }
        {
            var Q0;
            Q0 = qSketchRegion(id + "F0", true);
            extrude(context, id + "F1", {"entities" : qUnion([Q0]), "depth" : 2 * mm, "offsetDistance" : 25 * mm});
        }
    });
